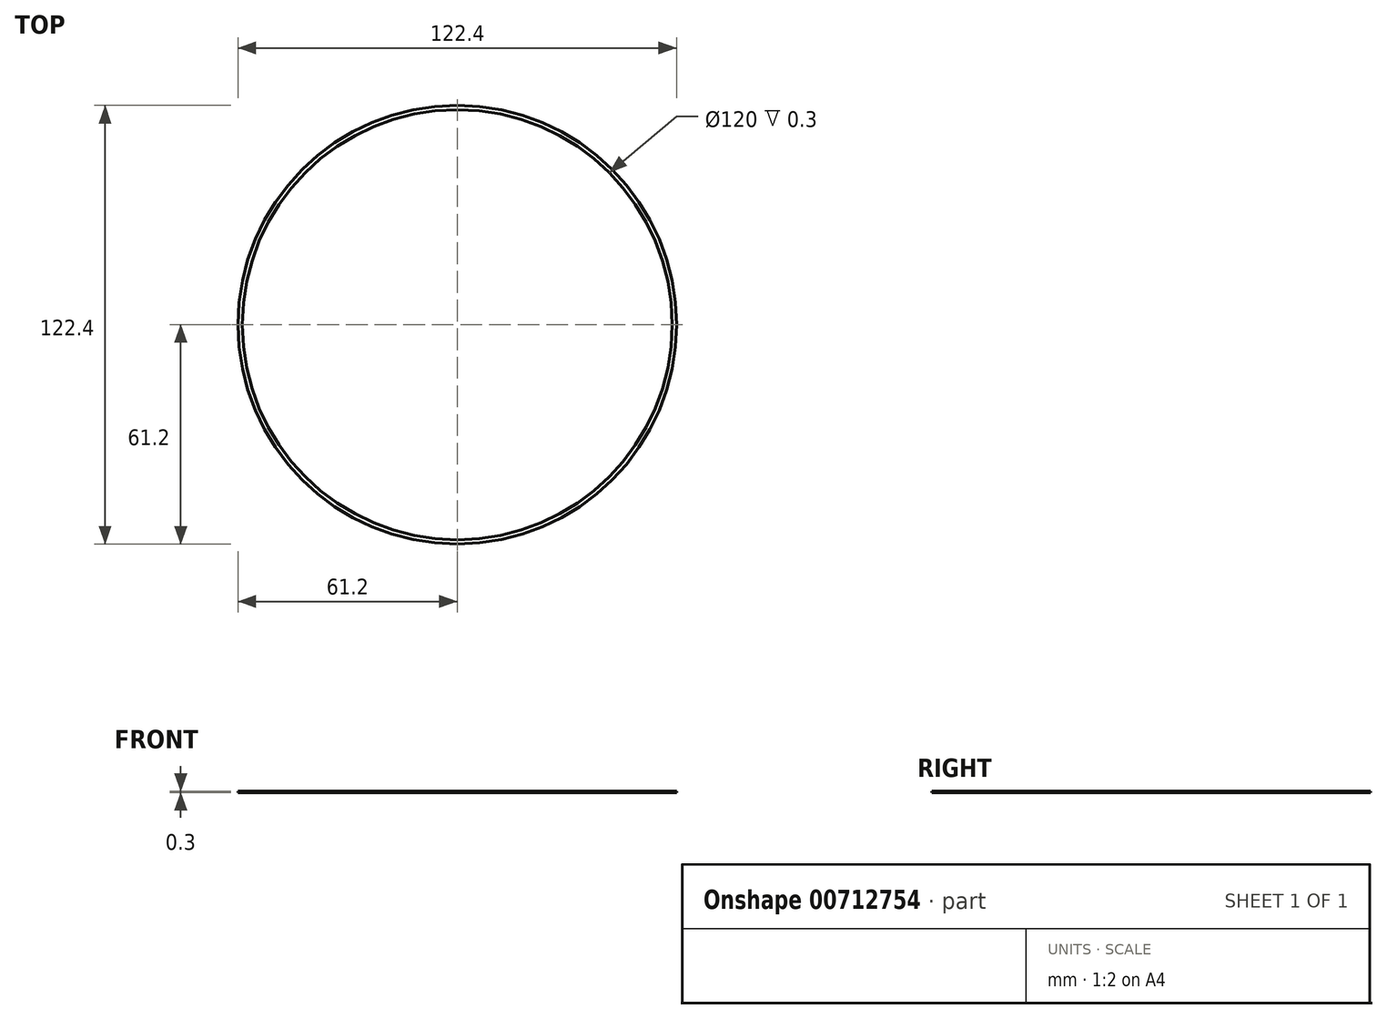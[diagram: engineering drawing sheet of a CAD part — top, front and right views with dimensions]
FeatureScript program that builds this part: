
annotation { "Feature Type Name" : "Feature", "Feature Type Description" : "" }
export const myFeature = defineFeature(function(context is Context, id is Id, definition is map)
    precondition{}
    {
        {
            var Q0;
            Q0=qCreatedBy(makeId("Top.planeOp"),FACE);
            var sketch = newSketch(context, id + "F0", { "sketchPlane" : qUnion([Q0])});
            skCircle(sketch, "E0", {"center": v(0, 0) * mm, "radius": 60 * mm});
            skCircle(sketch, "E1.0", {"center": v(0, 0) * mm, "radius": 61.2 * mm});
            skSolve(sketch);
        }
        {
            var Q0;
            Q0 = qSketchRegion(id + "F0", true);
            extrude(context, id + "F1", {"entities" : qUnion([Q0]), "depth" : 0.3 * mm, "offsetDistance" : 25 * mm});
        }
    });
